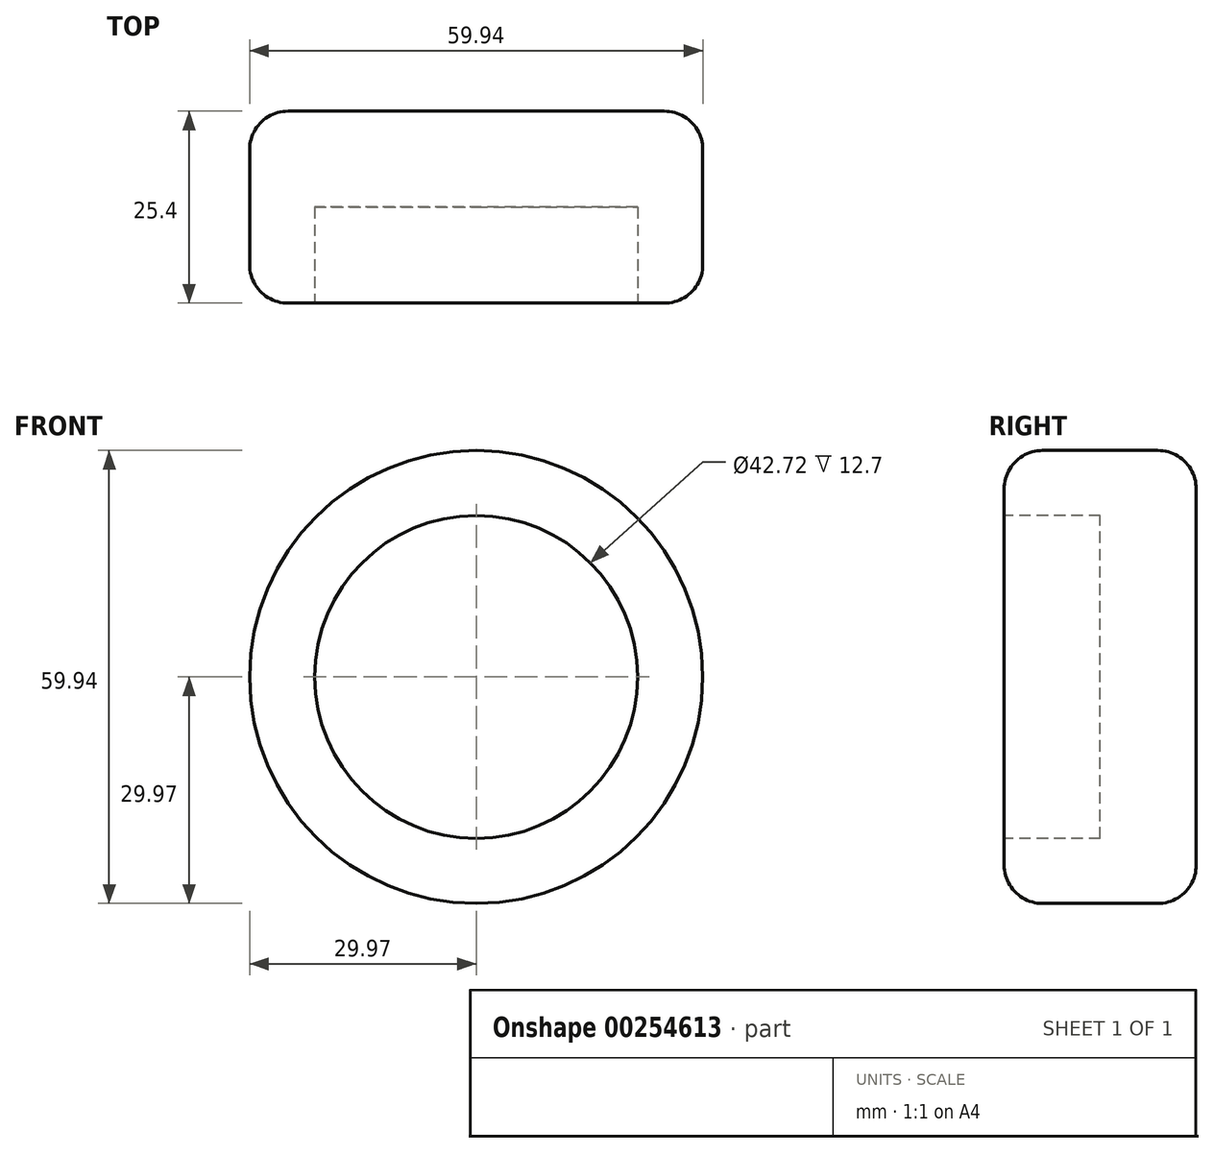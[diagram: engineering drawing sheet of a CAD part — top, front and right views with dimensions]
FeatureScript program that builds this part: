
annotation { "Feature Type Name" : "Feature", "Feature Type Description" : "" }
export const myFeature = defineFeature(function(context is Context, id is Id, definition is map)
    precondition{}
    {
        {
            var Q0;
            Q0=qCreatedBy(makeId("Front.planeOp"),FACE);
            var sketch = newSketch(context, id + "F0", { "sketchPlane" : qUnion([Q0])});
            skCircle(sketch, "E0", {"center": v(0, 0) * mm, "radius": 29.97 * mm});
            skSolve(sketch);
        }
        {
            var Q0;
            Q0 = qSketchRegion(id + "F0", true);
            extrude(context, id + "F1", {"entities" : qUnion([Q0]), "depth" : 25.4 * mm});
        }
        {
            var Q0;
            Q0=makeQuery(id+"F1.opExtrude","CAP_EDGE",EDGE,{"disambiguationData":[OSD([sQuery(id+"F0.wireOp",EDGE,"E0")])],"isStart":true});
            var Q1;
            Q1=makeQuery(id+"F1.opExtrude","CAP_EDGE",EDGE,{"disambiguationData":[OSD([sQuery(id+"F0.wireOp",EDGE,"E0")])],"isStart":false});
            fillet(context, id + "F2", {"entities" : qUnion([Q0, Q1]), "radius" : 5.08 * mm, "tangentPropagation" : true, "allowEdgeOverflow" : false});
        }
        {
            var Q0;
            Q0=makeQuery(id+"F1.opExtrude","CAP_FACE",FACE,{"disambiguationData":[OSD([sQuery(id+"F0.wireOp",EDGE,"E0")])],"isStart":false});
            var sketch = newSketch(context, id + "F3", { "sketchPlane" : qUnion([Q0])});
            skCircle(sketch, "E1", {"center": v(0, 0) * mm, "radius": 21.36 * mm});
            skSolve(sketch);
        }
        {
            var Q0;
            Q0 = qSketchRegion(id + "F3", true);
            extrude(context, id + "F4", {"entities" : qUnion([Q0]), "operationType" : NewBodyOperationType.REMOVE, "endBound" : BoundingType.SYMMETRIC, "oppositeDirection" : true, "depth" : 25.4 * mm});
        }
    });
